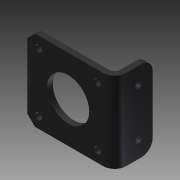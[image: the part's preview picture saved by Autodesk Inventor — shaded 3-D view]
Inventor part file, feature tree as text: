
AUTODESK INVENTOR PART (.ipt)
format: ipt  version: 2015 (Build 190159000, 159)  size: 175,616 bytes
history: native  units: mm
features: extrude x2, hole x2, fillet x1, chamfer x1, plane x1, other x1
ambient origin geometry x8: Origin, YZ Plane, XZ Plane, XY Plane, X Axis, Y Axis, Z Axis, Center Point
bodies: Solid1 (feature_tree)
feature tree (8):
  extrude  "Extrusión1"  Depth=20.0mm
  hole  "Agujero1"  [1 undecoded]
  hole  "Agujero2"  [1 undecoded]
  extrude  "Extrusión2"  Depth=42.5mm TaperAngle=0.0deg
  fillet  "Empalme1"  Radius=3.0mm
  chamfer  "Chaflán1"  Distance=25.0mm
  plane  "Plano de trabajo1"
  other  "Definición1"
note: 2 required parameter values undecoded (feature->parameter linkage not recoverable at this tier; creation-order binding heuristic only, values carry confidence <= 0.55)
